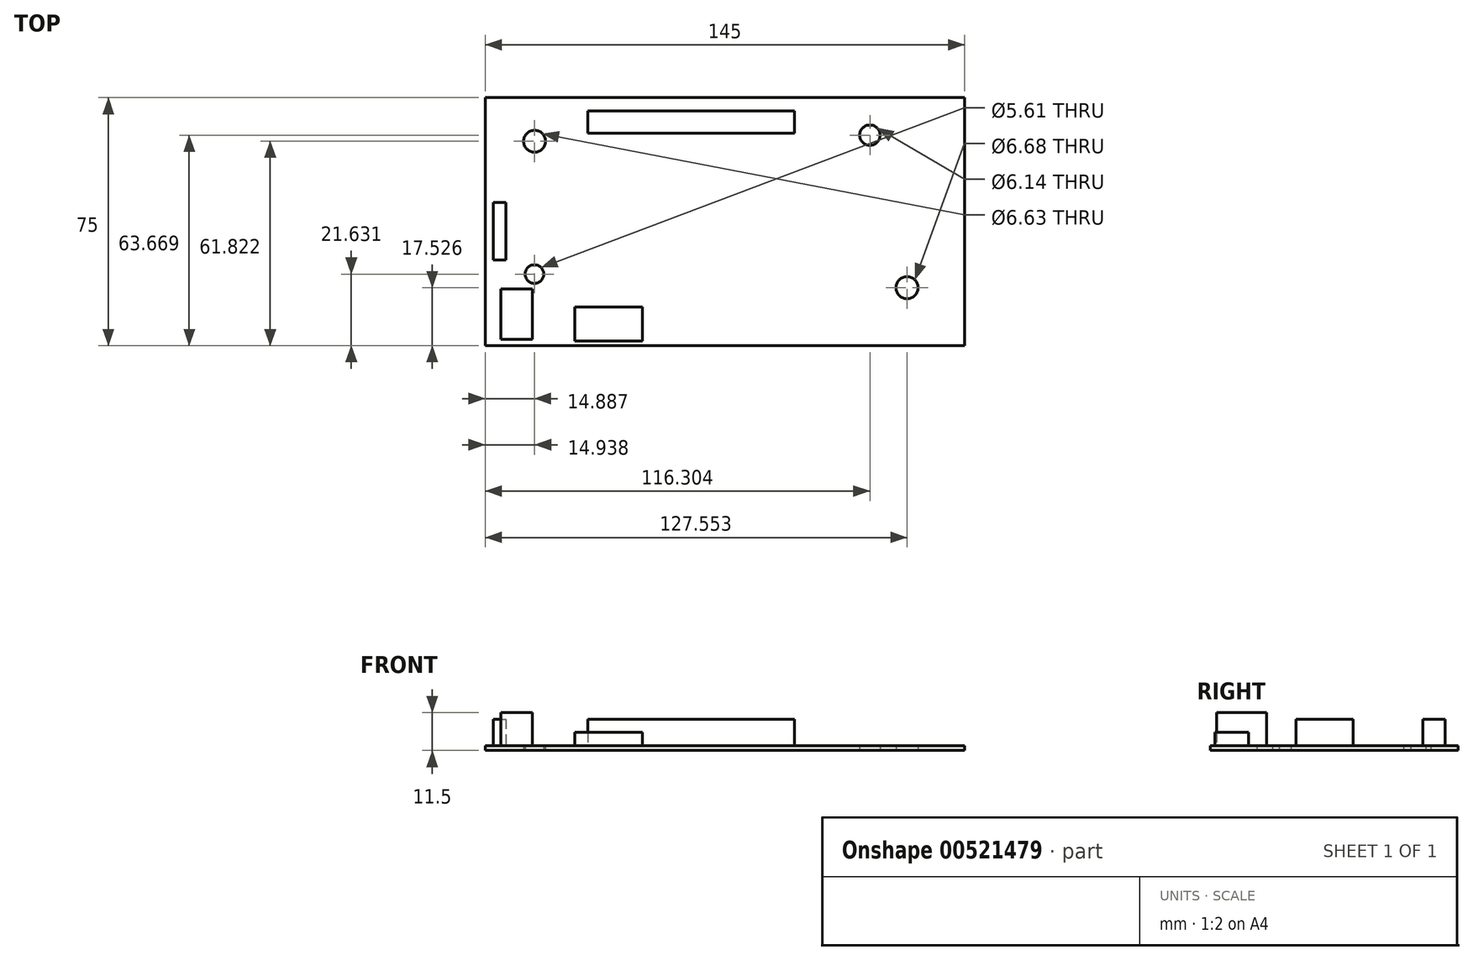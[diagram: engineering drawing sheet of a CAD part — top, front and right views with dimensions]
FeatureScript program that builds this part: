
annotation { "Feature Type Name" : "Feature", "Feature Type Description" : "" }
export const myFeature = defineFeature(function(context is Context, id is Id, definition is map)
    precondition{}
    {
        {
            var Q0;
            Q0=qCreatedBy(makeId("Top.planeOp"),FACE);
            var sketch = newSketch(context, id + "F0", { "sketchPlane" : qUnion([Q0])});
            skLineSegment(sketch, "E0.bottom", {"start": v(72.5, 37.5) * mm, "end": v(-72.5, 37.5) * mm});
            skLineSegment(sketch, "E0.top", {"start": v(72.5, -37.5) * mm, "end": v(-72.5, -37.5) * mm});
            skLineSegment(sketch, "E0.left", {"start": v(72.5, 37.5) * mm, "end": v(72.5, -37.5) * mm});
            skLineSegment(sketch, "E0.right", {"start": v(-72.5, 37.5) * mm, "end": v(-72.5, -37.5) * mm});
            skPoint(sketch, "E0.middle", {"position": v(0, 0) * mm});
            skCircle(sketch, "E1", {"center": v(43.8, 26.17) * mm, "radius": 3.07 * mm});
            skCircle(sketch, "E2", {"center": v(55.05, -19.97) * mm, "radius": 3.34 * mm});
            skCircle(sketch, "E3", {"center": v(-57.61, -15.87) * mm, "radius": 2.8 * mm});
            skCircle(sketch, "E4", {"center": v(-57.56, 24.32) * mm, "radius": 3.31 * mm});
            skSolve(sketch);
        }
        {
            var Q0;
            Q0 = qSketchRegion(id + "F0", true);
            extrude(context, id + "F1", {"entities" : qUnion([Q0]), "depth" : 1.5 * mm, "offsetDistance" : 25 * mm});
        }
        {
            var Q0;
            Q0=makeQuery(id+"F1.opExtrude","CAP_FACE",FACE,{"disambiguationData":[OSD([sQuery(id+"F0.wireOp",EDGE,"E0.bottom"),sQuery(id+"F0.wireOp",EDGE,"E0.top"),sQuery(id+"F0.wireOp",EDGE,"E0.left"),sQuery(id+"F0.wireOp",EDGE,"E0.right"),sQuery(id+"F0.wireOp",EDGE,"E1"),sQuery(id+"F0.wireOp",EDGE,"E2"),sQuery(id+"F0.wireOp",EDGE,"E3"),sQuery(id+"F0.wireOp",EDGE,"E4")])],"isStart":false});
            var sketch = newSketch(context, id + "F2", { "sketchPlane" : qUnion([Q0])});
            skLineSegment(sketch, "E5.bottom", {"start": v(-45.47, -36.08) * mm, "end": v(-25.03, -36.08) * mm});
            skLineSegment(sketch, "E5.top", {"start": v(-45.47, -25.85) * mm, "end": v(-25.03, -25.85) * mm});
            skLineSegment(sketch, "E5.left", {"start": v(-45.47, -36.08) * mm, "end": v(-45.47, -25.85) * mm});
            skLineSegment(sketch, "E5.right", {"start": v(-25.03, -36.08) * mm, "end": v(-25.03, -25.85) * mm});
            skPoint(sketch, "E5.middle", {"position": v(-35.25, -30.97) * mm});
            skLineSegment(sketch, "E6.bottom", {"start": v(-70.07, -11.56) * mm, "end": v(-66.26, -11.56) * mm});
            skLineSegment(sketch, "E6.top", {"start": v(-70.07, 5.77) * mm, "end": v(-66.26, 5.77) * mm});
            skLineSegment(sketch, "E6.left", {"start": v(-70.07, -11.56) * mm, "end": v(-70.07, 5.77) * mm});
            skLineSegment(sketch, "E6.right", {"start": v(-66.26, -11.56) * mm, "end": v(-66.26, 5.77) * mm});
            skPoint(sketch, "E6.middle", {"position": v(-68.17, -2.9) * mm});
            skLineSegment(sketch, "E7.bottom", {"start": v(-41.49, 33.49) * mm, "end": v(21.06, 33.49) * mm});
            skLineSegment(sketch, "E7.top", {"start": v(-41.49, 26.78) * mm, "end": v(21.06, 26.78) * mm});
            skLineSegment(sketch, "E7.left", {"start": v(-41.49, 33.49) * mm, "end": v(-41.49, 26.78) * mm});
            skLineSegment(sketch, "E7.right", {"start": v(21.06, 33.49) * mm, "end": v(21.06, 26.78) * mm});
            skLineSegment(sketch, "E8.bottom", {"start": v(-67.8, -35.57) * mm, "end": v(-58.18, -35.57) * mm});
            skLineSegment(sketch, "E8.top", {"start": v(-67.8, -20.42) * mm, "end": v(-58.18, -20.42) * mm});
            skLineSegment(sketch, "E8.left", {"start": v(-67.8, -35.57) * mm, "end": v(-67.8, -20.42) * mm});
            skLineSegment(sketch, "E8.right", {"start": v(-58.18, -35.57) * mm, "end": v(-58.18, -20.42) * mm});
            skSolve(sketch);
        }
        {
            var Q0;
            Q0=makeQuery(id+"F2.imprint","IMPRINT",FACE,{"disambiguationData":[TD([[makeQuery(id+"F2.imprint","IMPRINT",EDGE,{"derivedFrom":sQuery(id+"F2.wireOp",EDGE,"E5.bottom")}),1.0]])]});
            extrude(context, id + "F3", {"entities" : qUnion([Q0]), "operationType" : NewBodyOperationType.ADD, "depth" : 4 * mm, "offsetDistance" : 25 * mm});
        }
        {
            var Q0;
            Q0=makeQuery(id+"F2.imprint","IMPRINT",FACE,{"disambiguationData":[TD([[makeQuery(id+"F2.imprint","IMPRINT",EDGE,{"derivedFrom":sQuery(id+"F2.wireOp",EDGE,"E6.bottom")}),1.0]])]});
            var Q1;
            Q1=makeQuery(id+"F2.imprint","IMPRINT",FACE,{"disambiguationData":[TD([[makeQuery(id+"F2.imprint","IMPRINT",EDGE,{"derivedFrom":sQuery(id+"F2.wireOp",EDGE,"E7.bottom")}),-1.0]])]});
            extrude(context, id + "F4", {"entities" : qUnion([Q0, Q1]), "operationType" : NewBodyOperationType.ADD, "depth" : 8 * mm, "offsetDistance" : 25 * mm});
        }
        {
            var Q0;
            Q0=makeQuery(id+"F2.imprint","IMPRINT",FACE,{"disambiguationData":[TD([[makeQuery(id+"F2.imprint","IMPRINT",EDGE,{"derivedFrom":sQuery(id+"F2.wireOp",EDGE,"E8.bottom")}),1.0]])]});
            extrude(context, id + "F5", {"entities" : qUnion([Q0]), "operationType" : NewBodyOperationType.ADD, "depth" : 10 * mm, "offsetDistance" : 25 * mm});
        }
    });
